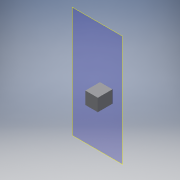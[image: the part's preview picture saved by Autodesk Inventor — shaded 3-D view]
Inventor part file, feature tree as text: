
AUTODESK INVENTOR PART (.ipt)
format: ipt  version: 2016 (Build 200138000, 138)  size: 92,160 bytes
history: native  units: in
note: dims shown in document units (in); Inventor stores cm internally (conversion verified against a paired STEP export)
features: plane x1, extrude x1, sketch x1, reference x1
ambient origin geometry x8: Origin, YZ Plane, XZ Plane, XY Plane, X Axis, Y Axis, Z Axis, Center Point
bodies: Solid1 (feature_tree)
feature tree (4):
  plane  "Work Plane1"
  extrude  "Extrusion1"  Depth=1.7in
  sketch  "Sketch1"  dims[d0=1.7in d1=1.7in d2=2.0in d3=0.0in]
  reference  "Reference1"
